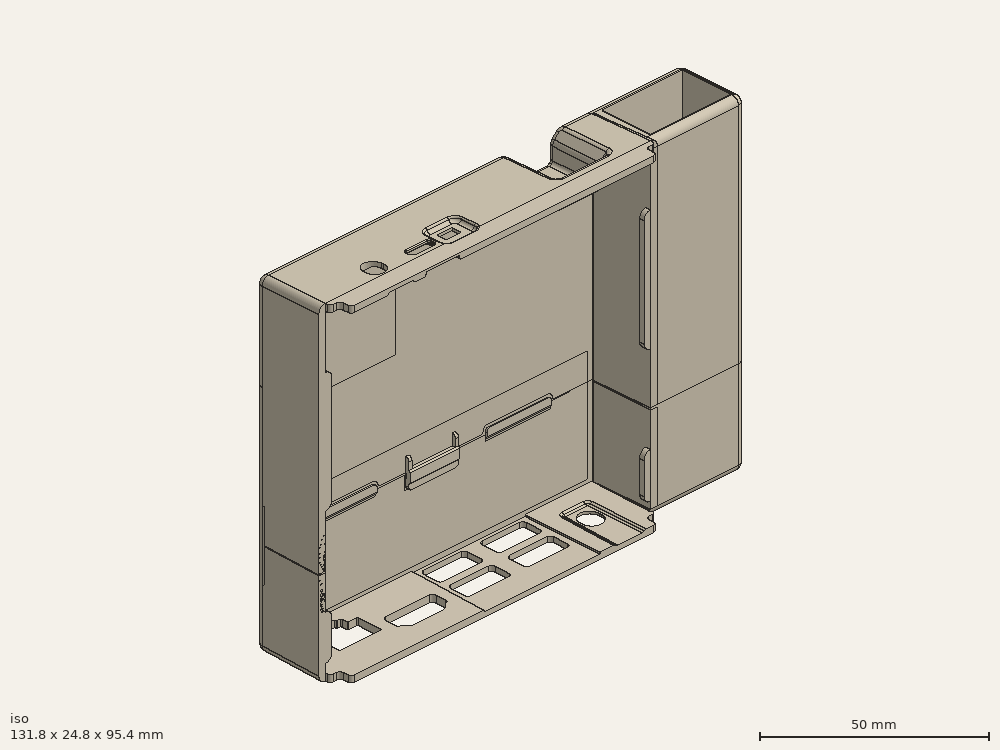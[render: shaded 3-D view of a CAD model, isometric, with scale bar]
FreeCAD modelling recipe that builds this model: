
FCSTD DOCUMENT  (FreeCAD 0.20R29177 +233 (Git))
Label: N2CaseOnePeice_10_12_2022
License: All rights reserved
LicenseURL: http://en.wikipedia.org/wiki/All_rights_reserved
objects: Part::Box×23, Part::Cylinder×12, Part::MultiFuse×10, Part::Cut×9, Part::Sphere×4, Part::Feature×2, Sketcher::SketchObject×2, PartDesign::Pad×2, PartDesign::Body×2
note: 68 computed .brp shape members not serialized (recipe doc carries the construction recipe); baked Part::Feature solids carry a one-line shape summary decoded from their .brp

FEATURE [Part::Feature] Solid  label="N2_BOTTOM_COVER"
  shape: bbox 104.6 x 25.21 x 71.78 mm, 343 faces (baked)
FEATURE [Part::Feature] Solid001  label="N2_TOP_COVER"
  shape: bbox 104.6 x 24.81 x 29.22 mm, 349 faces (baked)
FEATURE [Part::Box] Box  label="Cube"
  AttacherType = Attacher::AttachEngine3D
  Height = 15
  Length = 62.5
  Placement = pos=(-49,18,44) rot=(0,1,0;1.5708rad)
  Width = 2
FEATURE [Part::MultiFuse] Fusion  label="BottomCover"
  Shapes = -> [Solid,Box]
FEATURE [Part::Box] Box001  label="Cube001"
  AttacherType = Attacher::AttachEngine3D
  Height = 15
  Length = 97.5
  Placement = pos=(48.5,20,-3.5) rot=(0,1,0;3.14159rad)
  Width = 2
FEATURE [Part::Cut] Cut
  Base = -> Fusion
  Tool = -> Box001
FEATURE [Part::Box] Box002  label="usbEthernet"
  AttacherType = Attacher::AttachEngine3D
  Height = 25
  Length = 72
  Placement = pos=(52.5,2.6,47.4) rot=(0,1,0;1.5708rad)
  Width = 15
FEATURE [Part::Box] Box003  label="usbEthernetCover"
  AttacherType = Attacher::AttachEngine3D
  Height = 27.5
  Length = 72
  Placement = pos=(50.5,2.2,47.4) rot=(0,1,0;1.5708rad)
  Width = 15.85
FEATURE [Part::Box] Box004  label="usbEthernetCover001"
  AttacherType = Attacher::AttachEngine3D
  Height = 27.52
  Length = 65.19
  Placement = pos=(49.98,17.6,45.39) rot=(0,1,0;1.5708rad)
  Width = 2.4
FEATURE [Part::Box] Box005  label="usbEthernetCover002"
  AttacherType = Attacher::AttachEngine3D
  Height = 2
  Length = 65.19
  Placement = pos=(77.5,2.2,45.39) rot=(0,1,0;1.5708rad)
  Width = 15.8
FEATURE [Part::Cylinder] Cylinder
  Angle = 90
  AttacherType = Attacher::AttachEngine3D
  FirstAngle = 0
  Height = 65.2
  Placement = pos=(77.5,2.2,-19.8) rot=(0,0,-1;1.5708rad)
  Radius = 2
  SecondAngle = 0
FEATURE [Part::Cylinder] Cylinder001
  Angle = 90
  AttacherType = Attacher::AttachEngine3D
  FirstAngle = 0
  Height = 27.5
  Placement = pos=(77.5,18,45.4) rot=(0,-1,0;1.5708rad)
  Radius = 2
  SecondAngle = 0
FEATURE [Part::Cylinder] Cylinder002
  Angle = 90
  AttacherType = Attacher::AttachEngine3D
  FirstAngle = 0
  Height = 15.8
  Placement = pos=(77.5,2.2,45.4) rot=(0.57735,0.57735,0.57735;4.18879rad)
  Radius = 2
  SecondAngle = 0
FEATURE [Part::Cylinder] Cylinder003
  Angle = 90
  AttacherType = Attacher::AttachEngine3D
  FirstAngle = 0
  Height = 65.2
  Placement = pos=(77.5,18,-19.8) rot=(0,0,1;0rad)
  Radius = 2
  SecondAngle = 0
FEATURE [Part::Box] Box006  label="usbEthernetCover003"
  AttacherType = Attacher::AttachEngine3D
  Height = 27.2
  Length = 65.19
  Placement = pos=(50.3,0.2,45.39) rot=(0,1,0;1.5708rad)
  Width = 2.4
FEATURE [Part::Cylinder] Cylinder004
  Angle = 90
  AttacherType = Attacher::AttachEngine3D
  FirstAngle = 0
  Height = 26.4
  Placement = pos=(77.5,2.2,45.4) rot=(0.57735,-0.57735,-0.57735;2.0944rad)
  Radius = 2
  SecondAngle = 0
FEATURE [Part::Sphere] Sphere
  Angle1 = -90
  Angle2 = 90
  Angle3 = 360
  AttacherType = Attacher::AttachEngine3D
  Placement = pos=(77.5,18,45.4) rot=(0,0,1;0rad)
  Radius = 2
FEATURE [Part::Sphere] Sphere001
  Angle1 = -90
  Angle2 = 90
  Angle3 = 360
  AttacherType = Attacher::AttachEngine3D
  Placement = pos=(77.5,2.2,45.4) rot=(0,0,1;0rad)
  Radius = 2
FEATURE [Part::MultiFuse] Fusion001  label="usbCover"
  Shapes = -> [Box003,Box004,Box005,Cylinder,Cylinder001,Cylinder002,Cylinder003,Box006,Cylinder004,Sphere,Sphere001]
FEATURE [Part::MultiFuse] Fusion002
  Shapes = -> [Cut,Fusion001]
FEATURE [Part::Cut] Cut001  label="front"
  Base = -> Fusion002
  Tool = -> Box002
FEATURE [Part::Box] Box007  label="Cube002"
  AttacherType = Attacher::AttachEngine3D
  Height = 10
  Length = 30
  Placement = pos=(79.5,0,-19.8) rot=(0,1,0;3.14159rad)
  Width = 20
FEATURE [Part::Cut] Cut002
  Base = -> Cut001
  Tool = -> Box007
FEATURE [Part::Box] Box008  label="Cube003"
  AttacherType = Attacher::AttachEngine3D
  Height = 10
  Length = 30
  Placement = pos=(79.5,0,-19.8) rot=(0,1,0;3.14159rad)
  Width = 20
FEATURE [Part::Cut] Cut003  label="front001"
  Base = -> Cut002
  Tool = -> Box008
FEATURE [Part::Box] Box009  label="usbEthernet001"
  AttacherType = Attacher::AttachEngine3D
  Height = 25
  Length = 72
  Placement = pos=(52.5,2.6,6.3) rot=(0,1,0;1.5708rad)
  Width = 15
FEATURE [Part::Box] Box010  label="usbEthernetCover004"
  AttacherType = Attacher::AttachEngine3D
  Height = 27.5
  Length = 72
  Placement = pos=(50.5,2.2,-19.8) rot=(0,1,0;1.5708rad)
  Width = 15.85
FEATURE [Part::Box] Box011  label="usbEthernetCover005"
  AttacherType = Attacher::AttachEngine3D
  Height = 27.52
  Length = 65.19
  Placement = pos=(49.98,17.6,-19.8) rot=(0,1,0;1.5708rad)
  Width = 2.4
FEATURE [Part::Box] Box012  label="usbEthernetCover006"
  AttacherType = Attacher::AttachEngine3D
  Height = 2
  Length = 65.19
  Placement = pos=(77.5,2.2,-19.8) rot=(0,1,0;1.5708rad)
  Width = 15.8
FEATURE [Part::Box] Box013  label="usbEthernetCover007"
  AttacherType = Attacher::AttachEngine3D
  Height = 27.2
  Length = 65.19
  Placement = pos=(50.3,0.2,-19.8) rot=(0,1,0;1.5708rad)
  Width = 2.4
FEATURE [Part::Box] Box016  label="Cube005"
  AttacherType = Attacher::AttachEngine3D
  Height = 50
  Length = 29.5
  Placement = pos=(79.5,0,-45.4) rot=(0,1,0;3.14159rad)
  Width = 20
FEATURE [Part::MultiFuse] Fusion003
  Shapes = -> [Solid001,Box010,Box011,Box012,Box013]
FEATURE [Part::Cut] Cut004
  Base = -> Fusion003
  Tool = -> Box016
FEATURE [Part::Cut] Cut005
  Base = -> Cut004
  Tool = -> Box009
FEATURE [Part::Box] Box017  label="Cube006"
  AttacherType = Attacher::AttachEngine3D
  Height = 50
  Length = 23.5
  Placement = pos=(73.4,17.6,-45.39) rot=(0,1,0;3.14159rad)
  Width = 20
FEATURE [Part::Cut] Cut006
  Base = -> Cut005
  Tool = -> Box017
FEATURE [Part::Cylinder] Cylinder005
  Angle = 90
  AttacherType = Attacher::AttachEngine3D
  FirstAngle = 0
  Height = 65.2
  Placement = pos=(77.5,2.2,-45.4) rot=(0,0,-1;1.5708rad)
  Radius = 2
  SecondAngle = 0
FEATURE [Part::Cylinder] Cylinder006
  Angle = 90
  AttacherType = Attacher::AttachEngine3D
  FirstAngle = 0
  Height = 27.5
  Placement = pos=(77.5,18,-45.4) rot=(0,-1,0;1.5708rad)
  Radius = 2
  SecondAngle = 0
FEATURE [Part::Cylinder] Cylinder007
  Angle = 90
  AttacherType = Attacher::AttachEngine3D
  FirstAngle = 0
  Height = 15.8
  Placement = pos=(77.5,2.2,-45.4) rot=(-1,0,0;1.5708rad)
  Radius = 2
  SecondAngle = 0
FEATURE [Part::Cylinder] Cylinder008
  Angle = 90
  AttacherType = Attacher::AttachEngine3D
  FirstAngle = 0
  Height = 65.2
  Placement = pos=(77.5,18,-45.4) rot=(0,0,1;0rad)
  Radius = 2
  SecondAngle = 0
FEATURE [Part::Cylinder] Cylinder009
  Angle = 90
  AttacherType = Attacher::AttachEngine3D
  FirstAngle = 0
  Height = 27.6
  Placement = pos=(77.5,2.2,-45.4) rot=(0.707107,0,-0.707107;3.14159rad)
  Radius = 2
  SecondAngle = 0
FEATURE [Part::Cylinder] Cylinder010
  Angle = 90
  AttacherType = Attacher::AttachEngine3D
  FirstAngle = 0
  Height = 27.6
  Placement = pos=(77.5,18,-45.4) rot=(0.57735,0.57735,-0.57735;4.18879rad)
  Radius = 2
  SecondAngle = 0
FEATURE [Part::Box] Box018  label="Cube007"
  AttacherType = Attacher::AttachEngine3D
  Height = 2
  Length = 27.6
  Placement = pos=(49.9,18,-45.4) rot=(1,0,0;3.14159rad)
  Width = 15.8
FEATURE [Part::Box] Box019  label="usbEthernet002"
  AttacherType = Attacher::AttachEngine3D
  Height = 25
  Length = 72
  Placement = pos=(52.5,2.6,-2.5) rot=(0,1,0;1.5708rad)
  Width = 15
FEATURE [Part::Sphere] Sphere002
  Angle1 = -90
  Angle2 = 90
  Angle3 = 360
  AttacherType = Attacher::AttachEngine3D
  Placement = pos=(77.5,18,-45.4) rot=(0,0,1;0rad)
  Radius = 2
FEATURE [Part::Sphere] Sphere003
  Angle1 = -90
  Angle2 = 90
  Angle3 = 360
  AttacherType = Attacher::AttachEngine3D
  Placement = pos=(77.5,2.2,-45.4) rot=(0,0,1;0rad)
  Radius = 2
FEATURE [Part::Box] Box020  label="Cube008"
  AttacherType = Attacher::AttachEngine3D
  Height = 40
  Length = 10
  Placement = pos=(73.6,0,-19.8) rot=(0,0,1;0rad)
  Width = 22
FEATURE [Part::MultiFuse] Fusion004  label="cuts"
  Shapes = -> [Box020,Box019]
FEATURE [Part::MultiFuse] Fusion005
  Shapes = -> [Sphere003,Cut006,Cylinder005,Cylinder006,Cylinder007,Cylinder008,Cylinder009,Cylinder010,Box018,Sphere002]
FEATURE [Part::Cut] Cut007  label="back"
  Base = -> Fusion005
  Tool = -> Fusion004
FEATURE [Part::Box] Box021  label="Cube009"
  AttacherType = Attacher::AttachEngine3D
  Height = 32.5
  Length = 97.5
  Placement = pos=(48.5,18,-11.9) rot=(0,1,0;3.14159rad)
  Width = 2
FEATURE [Part::Box] Box068  label="logoBase001"
  AttacherType = Attacher::AttachEngine3D
  Height = 30
  Length = 35
  Placement = pos=(21.5,-44,15.25) rot=(0,0,1;0rad)
  Width = 1.8
FEATURE [Sketcher::SketchObject] Sketch001
  FullyConstrained = false
  MapMode = 5
  Support = -> [XY_Plane001]
  sketch-geometry (205):
    g0: LineSegment StartX=-15.0667 StartY=-2.9879 StartZ=0 EndX=-14.4175 EndY=-3.20194 EndZ=0
    g1: LineSegment StartX=-14.1386 StartY=-3.3581 StartZ=0 EndX=-13.8673 EndY=-3.55064 EndZ=0
    g2: LineSegment StartX=-10.8098 StartY=-4.00788 StartZ=0 EndX=-10.5716 EndY=-4.29909 EndZ=0
    g3: LineSegment StartX=-10.5716 StartY=-4.29909 StartZ=0 EndX=-10.1338 EndY=-4.33136 EndZ=0
    g4: LineSegment StartX=-10.1338 StartY=-4.33136 StartZ=0 EndX=-9.89036 EndY=-4.3898 EndZ=0
    g5: LineSegment StartX=-9.51656 StartY=-5.73022 StartZ=0 EndX=-9.24931 EndY=-5.76229 EndZ=0
    g6: LineSegment StartX=-9.24931 StartY=-5.76229 StartZ=0 EndX=-8.92861 EndY=-5.90126 EndZ=0
    g7: LineSegment StartX=-8.92861 StartY=-5.90126 StartZ=0 EndX=-8.54378 EndY=-5.86384 EndZ=0
    g8: LineSegment StartX=-8.54378 StartY=-5.86384 StartZ=0 EndX=-7.71788 EndY=-5.75845 EndZ=0
    g9: LineSegment StartX=-7.71788 StartY=-5.75845 StartZ=0 EndX=-7.37291 EndY=-5.97257 EndZ=0
    g10: LineSegment StartX=-7.37291 StartY=-5.97257 StartZ=0 EndX=-6.72487 EndY=-5.72038 EndZ=0
    g11: LineSegment StartX=-6.72487 StartY=-5.72038 StartZ=0 EndX=-6.27066 EndY=-5.69481 EndZ=0
    g12: LineSegment StartX=-6.27066 StartY=-5.69481 StartZ=0 EndX=-6.06223 EndY=-5.80493 EndZ=0
    g13: LineSegment StartX=-6.06223 StartY=-5.80493 StartZ=0 EndX=-5.35089 EndY=-5.48914 EndZ=0
    g14: LineSegment StartX=-5.35089 StartY=-5.48914 StartZ=0 EndX=-5.02402 EndY=-5.48914 EndZ=0
    g15: LineSegment StartX=-5.02402 StartY=-5.48914 StartZ=0 EndX=-4.80126 EndY=-5.53132 EndZ=0
    g16: LineSegment StartX=-4.80126 StartY=-5.53132 StartZ=0 EndX=-4.19735 EndY=-5.16248 EndZ=0
    g17: LineSegment StartX=-3.75191 StartY=-4.97251 StartZ=0 EndX=-3.37714 EndY=-4.97251 EndZ=0
    g18: LineSegment StartX=-3.37714 StartY=-4.97251 StartZ=0 EndX=-2.81898 EndY=-4.45422 EndZ=0
    g19: LineSegment StartX=-2.81898 StartY=-4.45422 StartZ=0 EndX=-2.62761 EndY=-4.34259 EndZ=0
    g20: LineSegment StartX=-2.62761 StartY=-4.34259 StartZ=0 EndX=-2.15112 EndY=-4.35765 EndZ=0
    g21: LineSegment StartX=-2.38042 StartY=-4.51801 StartZ=0 EndX=-3.18577 EndY=-5.42702 EndZ=0
    g22: LineSegment StartX=-3.18577 StartY=-5.42702 StartZ=0 EndX=-3.61318 EndY=-6.05824 EndZ=0
    g23: LineSegment StartX=-3.61318 StartY=-6.05824 StartZ=0 EndX=-3.7111 EndY=-6.64579 EndZ=0
    g24: LineSegment StartX=-3.7111 StartY=-6.64579 StartZ=0 EndX=-3.83514 EndY=-7.15501 EndZ=0
    g25: LineSegment StartX=-3.83514 StartY=-7.15501 StartZ=0 EndX=-3.75878 EndY=-7.50876 EndZ=0
    g26: LineSegment StartX=-3.75878 StartY=-7.50876 StartZ=0 EndX=-3.70596 EndY=-7.68135 EndZ=0
    g27: LineSegment StartX=-3.70596 StartY=-7.68135 StartZ=0 EndX=-3.53967 EndY=-7.85202 EndZ=0
    g28: LineSegment StartX=-3.53967 StartY=-7.85202 StartZ=0 EndX=-3.4685 EndY=-8.65617 EndZ=0
    g29: LineSegment StartX=-3.27268 StartY=-8.56671 StartZ=0 EndX=-3.16823 EndY=-8.76909 EndZ=0
    g30: LineSegment StartX=-3.07088 StartY=-9.32083 StartZ=0 EndX=-2.84207 EndY=-9.3355 EndZ=0
    g31: LineSegment StartX=-2.84207 StartY=-9.3355 StartZ=0 EndX=-2.45193 EndY=-10.0982 EndZ=0
    g32: LineSegment StartX=-2.45193 StartY=-10.0982 StartZ=0 EndX=-2.24953 EndY=-10.1304 EndZ=0
    g33: LineSegment StartX=-2.24953 StartY=-10.1304 StartZ=0 EndX=-0.96042 EndY=-11.8753 EndZ=0
    g34: LineSegment StartX=-0.96042 StartY=-11.8753 StartZ=0 EndX=-0.153326 EndY=-11.3889 EndZ=0
    g35: LineSegment StartX=-0.153326 StartY=-11.3889 StartZ=0 EndX=0.461347 EndY=-10.7689 EndZ=0
    g36: LineSegment StartX=0.461347 StartY=-10.7689 StartZ=0 EndX=0.669802 EndY=-10.7261 EndZ=0
    g37: LineSegment StartX=0.669802 StartY=-10.7261 StartZ=0 EndX=1.31724 EndY=-9.70998 EndZ=0
    g38: LineSegment StartX=1.31724 StartY=-9.70998 StartZ=0 EndX=1.51826 EndY=-9.65081 EndZ=0
    g39: LineSegment StartX=1.51826 StartY=-9.65081 StartZ=0 EndX=1.74022 EndY=-9.08937 EndZ=0
    g40: LineSegment StartX=1.74022 StartY=-9.08937 StartZ=0 EndX=2.02094 EndY=-9.04367 EndZ=0
    g41: LineSegment StartX=2.02094 StartY=-9.04367 StartZ=0 EndX=2.39306 EndY=-7.80327 EndZ=0
    g42: LineSegment StartX=2.39306 StartY=-7.80327 StartZ=0 EndX=2.58839 EndY=-7.69871 EndZ=0
    g43: LineSegment StartX=2.6542 StartY=-7.03945 StartZ=0 EndX=2.86963 EndY=-6.81749 EndZ=0
    g44: LineSegment StartX=2.86963 StartY=-6.81749 StartZ=0 EndX=3.0916 EndY=-6.92847 EndZ=0
    g45: LineSegment StartX=3.0916 StartY=-6.92847 StartZ=0 EndX=3.79666 EndY=-7.57478 EndZ=0
    g46: LineSegment StartX=3.79666 StartY=-7.57478 StartZ=0 EndX=3.93376 EndY=-7.50297 EndZ=0
    g47: LineSegment StartX=3.93376 StartY=-7.50297 StartZ=0 EndX=4.46256 EndY=-7.97301 EndZ=0
    g48: LineSegment StartX=4.46256 StartY=-7.97301 StartZ=0 EndX=4.68452 EndY=-7.92079 EndZ=0
    g49: LineSegment StartX=4.68452 StartY=-7.92079 StartZ=0 EndX=5.1154 EndY=-8.34513 EndZ=0
    g50: LineSegment StartX=5.1154 StartY=-8.34513 StartZ=0 EndX=5.32431 EndY=-8.28637 EndZ=0
    g51: LineSegment StartX=5.32431 StartY=-8.28637 StartZ=0 EndX=6.23668 EndY=-8.79564 EndZ=0
    g52: LineSegment StartX=6.23668 StartY=-8.79564 StartZ=0 EndX=6.50362 EndY=-8.76631 EndZ=0
    g53: LineSegment StartX=6.50362 StartY=-8.76631 StartZ=0 EndX=7.14802 EndY=-9.05537 EndZ=0
    g54: LineSegment StartX=7.14802 StartY=-9.05537 StartZ=0 EndX=8.04883 EndY=-9.18613 EndZ=0
    g55: LineSegment StartX=8.04883 StartY=-9.18613 StartZ=0 EndX=8.36847 EndY=-7.93662 EndZ=0
    g56: LineSegment StartX=8.36847 StartY=-7.93662 StartZ=0 EndX=8.49923 EndY=-7.79133 EndZ=0
    g57: LineSegment StartX=8.49923 StartY=-7.79133 StartZ=0 EndX=8.43477 EndY=-6.72206 EndZ=0
    g58: LineSegment StartX=8.43477 StartY=-6.72206 StartZ=0 EndX=8.58621 EndY=-6.47988 EndZ=0
    g59: LineSegment StartX=8.58621 StartY=-6.47988 StartZ=0 EndX=8.32296 EndY=-5.53178 EndZ=0
    g60: LineSegment StartX=8.32296 StartY=-5.53178 StartZ=0 EndX=8.43984 EndY=-5.19091 EndZ=0
    g61: LineSegment StartX=8.43984 StartY=-5.19091 StartZ=0 EndX=8.07426 EndY=-4.39307 EndZ=0
    g62: LineSegment StartX=8.07426 StartY=-4.39307 StartZ=0 EndX=8.04236 EndY=-4.17777 EndZ=0
    g63: LineSegment StartX=8.04236 StartY=-4.17777 StartZ=0 EndX=8.0902 EndY=-3.99438 EndZ=0
    g64: LineSegment StartX=8.4103 StartY=-4.11103 StartZ=0 EndX=8.72013 EndY=-4.0502 EndZ=0
    g65: LineSegment StartX=8.72013 StartY=-4.0502 StartZ=0 EndX=9.31817 EndY=-4.0502 EndZ=0
    g66: LineSegment StartX=9.31817 StartY=-4.0502 StartZ=0 EndX=9.82964 EndY=-4.15887 EndZ=0
    g67: LineSegment StartX=10.1326 StartY=-3.9675 StartZ=0 EndX=10.5175 EndY=-3.9623 EndZ=0
    g68: LineSegment StartX=10.5175 StartY=-3.9623 StartZ=0 EndX=10.8831 EndY=-3.97536 EndZ=0
    g69: LineSegment StartX=10.8831 StartY=-3.97536 StartZ=0 EndX=11.2245 EndY=-4.09431 EndZ=0
    g70: LineSegment StartX=11.2245 StartY=-4.09431 StartZ=0 EndX=11.6861 EndY=-3.91007 EndZ=0
    g71: LineSegment StartX=11.6861 StartY=-3.91007 StartZ=0 EndX=12.1039 EndY=-3.88396 EndZ=0
    g72: LineSegment StartX=12.1039 StartY=-3.88396 StartZ=0 EndX=12.6 EndY=-3.9623 EndZ=0
    g73: LineSegment StartX=12.6 StartY=-3.9623 StartZ=0 EndX=13.5793 EndY=-3.87743 EndZ=0
    g74: LineSegment StartX=13.5793 StartY=-3.87743 StartZ=0 EndX=14.3888 EndY=-3.74687 EndZ=0
    g75: LineSegment StartX=14.3888 StartY=-3.74687 StartZ=0 EndX=14.7544 EndY=-3.68158 EndZ=0
    g76: LineSegment StartX=14.7544 StartY=-3.68158 StartZ=0 EndX=15.2767 EndY=-3.75339 EndZ=0
    g77: LineSegment StartX=15.2767 StartY=-3.75339 StartZ=0 EndX=15.0432 EndY=-3.24137 EndZ=0
    g78: LineSegment StartX=15.0432 StartY=-3.24137 StartZ=0 EndX=14.5209 EndY=-2.51672 EndZ=0
    g79: LineSegment StartX=14.5209 StartY=-2.51672 StartZ=0 EndX=14.0378 EndY=-1.99445 EndZ=0
    g80: LineSegment StartX=14.0378 StartY=-1.99445 StartZ=0 EndX=13.2802 EndY=-1.54625 EndZ=0
    g81: LineSegment StartX=13.2802 StartY=-1.54625 StartZ=0 EndX=13.0438 EndY=-1.23117 EndZ=0
    g82: LineSegment StartX=13.0438 StartY=-1.23117 StartZ=0 EndX=12.1074 EndY=-0.797939 EndZ=0
    g83: LineSegment StartX=12.1074 StartY=-0.797939 StartZ=0 EndX=11.3804 EndY=-0.250878 EndZ=0
    g84: LineSegment StartX=11.3804 StartY=-0.250878 StartZ=0 EndX=10.4396 EndY=0.304889 EndZ=0
    g85: LineSegment StartX=10.4396 StartY=0.304889 StartZ=0 EndX=9.59526 EndY=0.727998 EndZ=0
    g86: LineSegment StartX=9.59526 StartY=0.727998 StartZ=0 EndX=8.53624 EndY=0.97306 EndZ=0
    g87: LineSegment StartX=8.53624 StartY=0.97306 StartZ=0 EndX=7.199 EndY=0.97306 EndZ=0
    g88: LineSegment StartX=7.199 StartY=0.97306 StartZ=0 EndX=5.77932 EndY=0.795578 EndZ=0
    g89: LineSegment StartX=5.77932 StartY=0.795578 StartZ=0 EndX=5.60186 EndY=0.795578 EndZ=0
    g90: LineSegment StartX=5.60186 StartY=0.795578 StartZ=0 EndX=5.83178 EndY=0.981815 EndZ=0
    g91: LineSegment StartX=5.83178 StartY=0.981815 StartZ=0 EndX=6.25403 EndY=1.1582 EndZ=0
    g92: LineSegment StartX=6.30214 StartY=1.38269 StartZ=0 EndX=7.17987 EndY=1.70686 EndZ=0
    g93: LineSegment StartX=7.17987 StartY=1.70686 StartZ=0 EndX=7.44682 EndY=1.79438 EndZ=0
    g94: LineSegment StartX=7.44682 StartY=1.79438 StartZ=0 EndX=7.49058 EndY=2.12696 EndZ=0
    g95: LineSegment StartX=7.49058 StartY=2.12696 StartZ=0 EndX=8.30058 EndY=2.66839 EndZ=0
    g96: LineSegment StartX=8.30058 StartY=2.66839 StartZ=0 EndX=8.68575 EndY=2.81854 EndZ=0
    g97: LineSegment StartX=8.68575 StartY=2.81854 StartZ=0 EndX=8.68575 EndY=3.12537 EndZ=0
    g98: LineSegment StartX=8.68575 StartY=3.12537 StartZ=0 EndX=8.89508 EndY=3.18684 EndZ=0
    g99: LineSegment StartX=8.89508 StartY=3.18684 StartZ=0 EndX=9.63492 EndY=4.06602 EndZ=0
    g100: LineSegment StartX=9.63492 StartY=4.06602 StartZ=0 EndX=9.62638 EndY=4.32743 EndZ=0
    g101: LineSegment StartX=9.62638 StartY=4.32743 StartZ=0 EndX=10.2068 EndY=5.18314 EndZ=0
    g102: LineSegment StartX=10.2068 StartY=5.18314 StartZ=0 EndX=9.25518 EndY=5.64445 EndZ=0
    g103: LineSegment StartX=9.1102 StartY=5.87597 StartZ=0 EndX=8.32132 EndY=5.97336 EndZ=0
    g104: LineSegment StartX=8.32132 StartY=5.97336 StartZ=0 EndX=8.15466 EndY=6.06625 EndZ=0
    g105: LineSegment StartX=7.63471 StartY=6.13088 StartZ=0 EndX=7.56391 EndY=6.33267 EndZ=0
    g106: LineSegment StartX=7.56391 StartY=6.33267 StartZ=0 EndX=6.74832 EndY=6.35496 EndZ=0
    g107: LineSegment StartX=6.74832 StartY=6.35496 StartZ=0 EndX=6.46819 EndY=6.29526 EndZ=0
    g108: LineSegment StartX=6.46819 StartY=6.29526 StartZ=0 EndX=6.27042 EndY=6.61061 EndZ=0
    g109: LineSegment StartX=6.27042 StartY=6.61061 StartZ=0 EndX=5.40453 EndY=6.33267 EndZ=0
    g110: LineSegment StartX=5.40453 StartY=6.33267 StartZ=0 EndX=5.27091 EndY=6.47164 EndZ=0
    g111: LineSegment StartX=5.27091 StartY=6.47164 StartZ=0 EndX=4.56942 EndY=6.24725 EndZ=0
    g112: LineSegment StartX=4.56942 StartY=6.24725 StartZ=0 EndX=4.44161 EndY=6.40652 EndZ=0
    g113: LineSegment StartX=4.44161 StartY=6.40652 StartZ=0 EndX=3.4195 EndY=5.94588 EndZ=0
    g114: LineSegment StartX=3.4195 StartY=5.94588 StartZ=0 EndX=3.29192 EndY=6.1532 EndZ=0
    g115: LineSegment StartX=3.29192 StartY=6.1532 StartZ=0 EndX=2.15964 EndY=5.49137 EndZ=0
    g116: LineSegment StartX=2.15964 StartY=5.49137 StartZ=0 EndX=2.00016 EndY=5.69869 EndZ=0
    g117: LineSegment StartX=2.00016 StartY=5.69869 StartZ=0 EndX=1.6185 EndY=5.34828 EndZ=0
    g118: LineSegment StartX=1.6185 StartY=5.34828 StartZ=0 EndX=1.45984 EndY=5.94974 EndZ=0
    g119: LineSegment StartX=1.38165 StartY=6.28651 StartZ=0 EndX=1.14534 EndY=6.29963 EndZ=0
    g120: LineSegment StartX=0.348522 StartY=7.29544 StartZ=0 EndX=0.126706 EndY=7.68126 EndZ=0
    g121: LineSegment StartX=0.126706 StartY=7.68126 StartZ=0 EndX=-0.415308 EndY=8.18163 EndZ=0
    g122: LineSegment StartX=-0.415308 StartY=8.18163 StartZ=0 EndX=-0.872658 EndY=8.6237 EndZ=0
    g123: LineSegment StartX=-0.872658 StartY=8.6237 StartZ=0 EndX=-1.12074 EndY=8.64329 EndZ=0
    g124: LineSegment StartX=-1.12074 StartY=8.64329 StartZ=0 EndX=-1.79316 EndY=9.11986 EndZ=0
    g125: LineSegment StartX=-1.79316 StartY=9.11986 StartZ=0 EndX=-2.31488 EndY=9.12122 EndZ=0
    g126: LineSegment StartX=-2.31488 StartY=9.12122 StartZ=0 EndX=-2.71321 EndY=9.13846 EndZ=0
    g127: LineSegment StartX=-2.71321 StartY=9.13846 StartZ=0 EndX=-2.88425 EndY=9.34157 EndZ=0
    g128: LineSegment StartX=-2.88425 StartY=9.34157 StartZ=0 EndX=-3.16779 EndY=9.26454 EndZ=0
    g129: LineSegment StartX=-3.70739 StartY=9.82796 StartZ=0 EndX=-4.04915 EndY=9.7003 EndZ=0
    g130: LineSegment StartX=-4.04915 StartY=9.7003 StartZ=0 EndX=-4.42988 EndY=10.011 EndZ=0
    g131: LineSegment StartX=-5.98947 StartY=10.3656 StartZ=0 EndX=-7.32605 EndY=10.4108 EndZ=0
    g132: LineSegment StartX=-7.25254 StartY=9.13254 StartZ=0 EndX=-7.36878 EndY=8.7693 EndZ=0
    g133: LineSegment StartX=-7.36878 StartY=8.7693 StartZ=0 EndX=-7.2614 EndY=7.83762 EndZ=0
    g134: LineSegment StartX=-7.2614 StartY=7.83762 StartZ=0 EndX=-7.41112 EndY=7.6042 EndZ=0
    g135: LineSegment StartX=-7.41112 StartY=7.6042 StartZ=0 EndX=-7.09216 EndY=6.74302 EndZ=0
    g136: LineSegment StartX=-7.09216 StartY=6.74302 StartZ=0 EndX=-7.10014 EndY=6.55962 EndZ=0
    g137: LineSegment StartX=-7.10014 StartY=6.55962 StartZ=0 EndX=-7.29151 EndY=6.3842 EndZ=0
    g138: LineSegment StartX=-7.29151 StartY=6.3842 StartZ=0 EndX=-6.74132 EndY=5.29976 EndZ=0
    g139: LineSegment StartX=-6.74132 StartY=5.29976 StartZ=0 EndX=-6.87495 EndY=5.02732 EndZ=0
    g140: LineSegment StartX=-6.87495 StartY=5.02732 StartZ=0 EndX=-6.31586 EndY=4.42065 EndZ=0
    g141: LineSegment StartX=-6.31586 StartY=4.42065 StartZ=0 EndX=-6.30396 EndY=4.19463 EndZ=0
    g142: LineSegment StartX=-6.30396 StartY=4.19463 StartZ=0 EndX=-6.05415 EndY=4.0043 EndZ=0
    g143: LineSegment StartX=-6.05415 StartY=4.0043 StartZ=0 EndX=-6.18501 EndY=3.95672 EndZ=0
    g144: LineSegment StartX=-6.18501 StartY=3.95672 StartZ=0 EndX=-5.54265 EndY=3.07645 EndZ=0
    g145: LineSegment StartX=-5.54265 StartY=3.07645 StartZ=0 EndX=-5.57833 EndY=2.90991 EndZ=0
    g146: LineSegment StartX=-5.57833 StartY=2.90991 StartZ=0 EndX=-5.1263 EndY=2.41029 EndZ=0
    g147: LineSegment StartX=-5.1263 StartY=2.41029 StartZ=0 EndX=-5.18578 EndY=2.26755 EndZ=0
    g148: LineSegment StartX=-5.18578 StartY=2.26755 StartZ=0 EndX=-4.73375 EndY=1.89878 EndZ=0
    g149: LineSegment StartX=-4.73375 StartY=1.89878 StartZ=0 EndX=-4.42446 EndY=1.5895 EndZ=0
    g150: LineSegment StartX=-4.42446 StartY=1.5895 StartZ=0 EndX=-5.31663 EndY=1.29211 EndZ=0
    g151: LineSegment StartX=-5.31663 StartY=1.29211 StartZ=0 EndX=-5.84004 EndY=1.08988 EndZ=0
    g152: LineSegment StartX=-5.84004 StartY=1.08988 StartZ=0 EndX=-6.04226 EndY=0.792495 EndZ=0
    g153: LineSegment StartX=-6.04226 StartY=0.792495 StartZ=0 EndX=-6.94632 EndY=0.994719 EndZ=0
    g154: LineSegment StartX=-6.94632 StartY=0.994719 StartZ=0 EndX=-7.19613 EndY=0.887659 EndZ=0
    g155: LineSegment StartX=-7.19613 StartY=0.887659 StartZ=0 EndX=-7.8147 EndY=1.0423 EndZ=0
    g156: LineSegment StartX=-7.8147 StartY=1.0423 StartZ=0 EndX=-8.02502 EndY=0.969153 EndZ=0
    g157: LineSegment StartX=-8.02502 StartY=0.969153 StartZ=0 EndX=-8.60267 EndY=1.03042 EndZ=0
    g158: LineSegment StartX=-8.60267 StartY=1.03042 StartZ=0 EndX=-8.8346 EndY=0.872878 EndZ=0
    g159: LineSegment StartX=-8.8346 StartY=0.872878 StartZ=0 EndX=-9.33349 EndY=0.929767 EndZ=0
    g160: LineSegment StartX=-9.33349 StartY=0.929767 StartZ=0 EndX=-9.66169 EndY=0.649695 EndZ=0
    g161: LineSegment StartX=-9.66169 StartY=0.649695 StartZ=0 EndX=-10.3249 EndY=0.649695 EndZ=0
    g162: LineSegment StartX=-10.3249 StartY=0.649695 StartZ=0 EndX=-11.0107 EndY=0.32425 EndZ=0
    g163: LineSegment StartX=-11.0107 StartY=0.32425 StartZ=0 EndX=-11.7283 EndY=0.053139 EndZ=0
    g164: LineSegment StartX=-11.7283 StartY=0.053139 StartZ=0 EndX=-12.2971 EndY=-0.13161 EndZ=0
    g165: LineSegment StartX=-12.2971 StartY=-0.13161 StartZ=0 EndX=-12.4212 EndY=-0.347049 EndZ=0
    g166: LineSegment StartX=-12.4212 StartY=-0.347049 StartZ=0 EndX=-13.296 EndY=-0.817096 EndZ=0
    g167: LineSegment StartX=-13.296 StartY=-0.817096 StartZ=0 EndX=-13.9227 EndY=-1.24144 EndZ=0
    g168: LineSegment StartX=-13.9227 StartY=-1.24144 StartZ=0 EndX=-14.1708 EndY=-1.59398 EndZ=0
    g169: LineSegment StartX=-14.1708 StartY=-1.59398 StartZ=0 EndX=-14.5386 EndY=-2.09216 EndZ=0
    g170: LineSegment StartX=-14.5386 StartY=-2.09216 StartZ=0 EndX=-14.7831 EndY=-2.4577 EndZ=0
    g171: LineSegment StartX=-14.7831 StartY=-2.4577 StartZ=0 EndX=-15.0667 EndY=-2.9879 EndZ=0
    g172: LineSegment StartX=7.82861 StartY=6.04487 StartZ=0 EndX=7.63471 EndY=6.13088 EndZ=0
    g173: LineSegment StartX=-14.4175 StartY=-3.20194 StartZ=0 EndX=-14.1386 EndY=-3.3581 EndZ=0
    g174: LineSegment StartX=-13.8673 StartY=-3.55064 StartZ=0 EndX=-13.4107 EndY=-3.57136 EndZ=0
    g175: LineSegment StartX=-13.1321 StartY=-3.61699 StartZ=0 EndX=-12.817 EndY=-3.62343 EndZ=0
    g176: LineSegment StartX=-12.817 StartY=-3.62343 StartZ=0 EndX=-12.4662 EndY=-3.85302 EndZ=0
    g177: LineSegment StartX=-13.4107 StartY=-3.57136 StartZ=0 EndX=-13.1321 EndY=-3.61699 EndZ=0
    g178: LineSegment StartX=-12.4662 StartY=-3.85302 StartZ=0 EndX=-11.8704 EndY=-3.85302 EndZ=0
    g179: LineSegment StartX=-11.8704 StartY=-3.85302 StartZ=0 EndX=-11.5204 EndY=-4.00836 EndZ=0
    g180: LineSegment StartX=-11.5204 StartY=-4.00836 StartZ=0 EndX=-11.1389 EndY=-4.05555 EndZ=0
    g181: LineSegment StartX=-11.1389 StartY=-4.05555 StartZ=0 EndX=-10.8098 EndY=-4.00788 EndZ=0
    g182: LineSegment StartX=-9.89036 StartY=-4.3898 StartZ=0 EndX=-9.99555 EndY=-4.87697 EndZ=0
    g183: LineSegment StartX=-9.99555 StartY=-4.87697 StartZ=0 EndX=-10.0894 EndY=-5.36391 EndZ=0
    g184: LineSegment StartX=-10.0894 StartY=-5.36391 StartZ=0 EndX=-10.107 EndY=-5.50471 EndZ=0
    g185: LineSegment StartX=-10.107 StartY=-5.50471 StartZ=0 EndX=-9.77848 EndY=-5.63965 EndZ=0
    g186: LineSegment StartX=-9.77848 StartY=-5.63965 StartZ=0 EndX=-9.51656 EndY=-5.73022 EndZ=0
    g187: LineSegment StartX=-4.19735 StartY=-5.16248 StartZ=0 EndX=-3.75191 EndY=-4.97251 EndZ=0
    g188: LineSegment StartX=-2.38042 StartY=-4.51801 StartZ=0 EndX=-2.15112 EndY=-4.35765 EndZ=0
    g189: LineSegment StartX=-3.4685 StartY=-8.65617 StartZ=0 EndX=-3.27268 EndY=-8.56671 EndZ=0
    g190: LineSegment StartX=-3.16823 StartY=-8.76909 StartZ=0 EndX=-3.07088 EndY=-9.32083 EndZ=0
    g191: LineSegment StartX=2.58839 StartY=-7.69871 StartZ=0 EndX=2.6542 EndY=-7.03945 EndZ=0
    g192: LineSegment StartX=8.0902 StartY=-3.99438 StartZ=0 EndX=8.4103 EndY=-4.11103 EndZ=0
    g193: LineSegment StartX=9.82964 StartY=-4.15887 StartZ=0 EndX=10.1326 EndY=-3.9675 EndZ=0
    g194: LineSegment StartX=6.30214 StartY=1.38269 StartZ=0 EndX=6.25403 EndY=1.1582 EndZ=0
    g195: LineSegment StartX=1.38165 StartY=6.28651 StartZ=0 EndX=1.45984 EndY=5.94974 EndZ=0
    g196: LineSegment StartX=0.348522 StartY=7.29544 StartZ=0 EndX=0.824344 EndY=6.91479 EndZ=0
    g197: LineSegment StartX=0.824344 StartY=6.91479 StartZ=0 EndX=1.14534 EndY=6.29963 EndZ=0
    g198: LineSegment StartX=-3.70739 StartY=9.82796 StartZ=0 EndX=-3.16779 EndY=9.26454 EndZ=0
    g199: LineSegment StartX=-5.98947 StartY=10.3656 StartZ=0 EndX=-5.43038 EndY=10.4489 EndZ=0
    g200: LineSegment StartX=-5.43038 StartY=10.4489 StartZ=0 EndX=-4.9791 EndY=10.1425 EndZ=0
    g201: LineSegment StartX=-4.42988 StartY=10.011 StartZ=0 EndX=-4.9791 EndY=10.1425 EndZ=0
    g202: LineSegment StartX=-7.25254 StartY=9.13254 StartZ=0 EndX=-7.32605 EndY=10.4108 EndZ=0
    g203: LineSegment StartX=7.82861 StartY=6.04487 StartZ=0 EndX=8.15466 EndY=6.06625 EndZ=0
    g204: LineSegment StartX=9.1102 StartY=5.87597 StartZ=0 EndX=9.25518 EndY=5.64445 EndZ=0
  constraints (114):
    c: Coincident(g4,g3)
    c: Coincident(g6,g5)
    c: Coincident(g8,g7)
    c: Coincident(g9,g8)
    c: Coincident(g10,g9)
    c: Coincident(g11,g10)
    c: Coincident(g13,g12)
    c: Coincident(g16,g15)
    c: Coincident(g22,g21)
    c: Coincident(g25,g24)
    c: Coincident(g26,g25)
    c: Coincident(g28,g27)
    c: Coincident(g33,g32)
    c: Coincident(g37,g36)
    c: Coincident(g38,g37)
    c: Coincident(g40,g39)
    c: Coincident(g44,g43)
    c: Coincident(g51,g50)
    c: Coincident(g52,g51)
    c: Coincident(g57,g56)
    c: Coincident(g58,g57)
    c: Coincident(g59,g58)
    c: Coincident(g61,g60)
    c: Coincident(g63,g62)
    c: Coincident(g66,g65)
    c: Coincident(g70,g69)
    c: Coincident(g72,g71)
    c: Coincident(g73,g72)
    c: Coincident(g74,g73)
    c: Coincident(g77,g76)
    c: Coincident(g80,g79)
    c: Coincident(g81,g80)
    c: Coincident(g83,g82)
    c: Coincident(g85,g84)
    c: Coincident(g86,g85)
    c: Coincident(g87,g86)
    c: Coincident(g89,g88)
    c: Coincident(g90,g89)
    c: Coincident(g91,g90)
    c: Coincident(g93,g92)
    c: Coincident(g95,g94)
    c: Coincident(g97,g96)
    c: Coincident(g98,g97)
    c: Coincident(g99,g98)
    c: Coincident(g100,g99)
    c: Coincident(g104,g103)
    c: Coincident(g106,g105)
    c: Coincident(g107,g106)
    c: Coincident(g111,g110)
    c: Coincident(g113,g112)
    c: Coincident(g118,g117)
    c: Coincident(g122,g121)
    c: Coincident(g126,g125)
    c: Coincident(g130,g129)
    c: Coincident(g133,g132)
    c: Coincident(g134,g133)
    c: Coincident(g135,g134)
    c: Coincident(g139,g138)
    c: Coincident(g142,g141)
    c: Coincident(g156,g155)
    c: Coincident(g157,g156)
    c: Coincident(g159,g158)
    c: Coincident(g161,g160)
    c: Coincident(g164,g163)
    c: Coincident(g165,g164)
    c: Coincident(g168,g167)
    c: Coincident(g169,g168)
    c: Coincident(g171,g170)
    c: Coincident(g171,g0)
    c: Coincident(g172,g105)
    c: DistanceX(g165) = -12.4212
    c: DistanceY(g165) = -0.347049
    c: Coincident(g173,g0)
    c: Coincident(g173,g1)
    c: Coincident(g174,g1)
    c: Coincident(g177,g174)
    c: Coincident(g177,g175)
    c: Coincident(g178,g176)
    c: Coincident(g181,g2)
    c: Coincident(g182,g4)
    c: Coincident(g186,g185)
    c: Coincident(g186,g5)
    c: Coincident(g187,g16)
    c: Coincident(g187,g17)
    c: Coincident(g188,g21)
    c: Coincident(g188,g20)
    c: Coincident(g189,g28)
    c: Coincident(g189,g29)
    c: Coincident(g190,g29)
    c: Coincident(g190,g30)
    c: Coincident(g191,g42)
    c: Coincident(g191,g43)
    c: Coincident(g192,g63)
    c: Coincident(g192,g64)
    c: Coincident(g193,g66)
    c: Coincident(g193,g67)
    c: Coincident(g194,g92)
    c: Coincident(g194,g91)
    c: Coincident(g195,g119)
    c: Coincident(g195,g118)
    c: Coincident(g196,g120)
    c: Coincident(g197,g119)
    c: Coincident(g198,g129)
    c: Coincident(g198,g128)
    c: Coincident(g199,g131)
    c: Coincident(g200,g199)
    c: Coincident(g201,g130)
    c: Coincident(g201,g200)
    c: Coincident(g202,g132)
    c: Coincident(g202,g131)
    c: Coincident(g203,g172)
    c: Coincident(g203,g104)
    c: Coincident(g204,g103)
    c: Coincident(g204,g102)
FEATURE [PartDesign::Pad] Pad001
  Direction = (0,0,1)
  Length = 3
  Length2 = 10
  Profile = -> Sketch001
  ReferenceAxis = -> Sketch001 [N_Axis]
  Type = 0
FEATURE [PartDesign::Body] Body001  label="logo002"
  Group = -> [Sketch001,Pad001]
  Origin = -> Origin001
  Placement = pos=(39.35,-43,30) rot=(1,0,0;1.5708rad)
  Tip = -> Pad001
FEATURE [Part::MultiFuse] Fusion040  label="logo003"
  Placement = pos=(-69,-26,58) rot=(1,0,0;3.14159rad)
  Shapes = -> [Body001,Box068]
FEATURE [Part::Cut] Cut008  label="front002"
  Base = -> Cut003
  Tool = -> Fusion040
FEATURE [Part::Box] Box069  label="logoBase002"
  AttacherType = Attacher::AttachEngine3D
  Height = 30
  Length = 35
  Placement = pos=(21.5,-44,15.25) rot=(0,0,1;0rad)
  Width = 1.8
FEATURE [Sketcher::SketchObject] Sketch002
  FullyConstrained = false
  MapMode = 5
  Support = -> [XY_Plane002]
  sketch-geometry (205):
    g0: LineSegment StartX=-15.0667 StartY=-2.9879 StartZ=0 EndX=-14.4175 EndY=-3.20194 EndZ=0
    g1: LineSegment StartX=-14.1386 StartY=-3.3581 StartZ=0 EndX=-13.8673 EndY=-3.55064 EndZ=0
    g2: LineSegment StartX=-10.8098 StartY=-4.00788 StartZ=0 EndX=-10.5716 EndY=-4.29909 EndZ=0
    g3: LineSegment StartX=-10.5716 StartY=-4.29909 StartZ=0 EndX=-10.1338 EndY=-4.33136 EndZ=0
    g4: LineSegment StartX=-10.1338 StartY=-4.33136 StartZ=0 EndX=-9.89036 EndY=-4.3898 EndZ=0
    g5: LineSegment StartX=-9.51656 StartY=-5.73022 StartZ=0 EndX=-9.24931 EndY=-5.76229 EndZ=0
    g6: LineSegment StartX=-9.24931 StartY=-5.76229 StartZ=0 EndX=-8.92861 EndY=-5.90126 EndZ=0
    g7: LineSegment StartX=-8.92861 StartY=-5.90126 StartZ=0 EndX=-8.54378 EndY=-5.86384 EndZ=0
    g8: LineSegment StartX=-8.54378 StartY=-5.86384 StartZ=0 EndX=-7.71788 EndY=-5.75845 EndZ=0
    g9: LineSegment StartX=-7.71788 StartY=-5.75845 StartZ=0 EndX=-7.37291 EndY=-5.97257 EndZ=0
    g10: LineSegment StartX=-7.37291 StartY=-5.97257 StartZ=0 EndX=-6.72487 EndY=-5.72038 EndZ=0
    g11: LineSegment StartX=-6.72487 StartY=-5.72038 StartZ=0 EndX=-6.27066 EndY=-5.69481 EndZ=0
    g12: LineSegment StartX=-6.27066 StartY=-5.69481 StartZ=0 EndX=-6.06223 EndY=-5.80493 EndZ=0
    g13: LineSegment StartX=-6.06223 StartY=-5.80493 StartZ=0 EndX=-5.35089 EndY=-5.48914 EndZ=0
    g14: LineSegment StartX=-5.35089 StartY=-5.48914 StartZ=0 EndX=-5.02402 EndY=-5.48914 EndZ=0
    g15: LineSegment StartX=-5.02402 StartY=-5.48914 StartZ=0 EndX=-4.80126 EndY=-5.53132 EndZ=0
    g16: LineSegment StartX=-4.80126 StartY=-5.53132 StartZ=0 EndX=-4.19735 EndY=-5.16248 EndZ=0
    g17: LineSegment StartX=-3.75191 StartY=-4.97251 StartZ=0 EndX=-3.37714 EndY=-4.97251 EndZ=0
    g18: LineSegment StartX=-3.37714 StartY=-4.97251 StartZ=0 EndX=-2.81898 EndY=-4.45422 EndZ=0
    g19: LineSegment StartX=-2.81898 StartY=-4.45422 StartZ=0 EndX=-2.62761 EndY=-4.34259 EndZ=0
    g20: LineSegment StartX=-2.62761 StartY=-4.34259 StartZ=0 EndX=-2.15112 EndY=-4.35765 EndZ=0
    g21: LineSegment StartX=-2.38042 StartY=-4.51801 StartZ=0 EndX=-3.18577 EndY=-5.42702 EndZ=0
    g22: LineSegment StartX=-3.18577 StartY=-5.42702 StartZ=0 EndX=-3.61318 EndY=-6.05824 EndZ=0
    g23: LineSegment StartX=-3.61318 StartY=-6.05824 StartZ=0 EndX=-3.7111 EndY=-6.64579 EndZ=0
    g24: LineSegment StartX=-3.7111 StartY=-6.64579 StartZ=0 EndX=-3.83514 EndY=-7.15501 EndZ=0
    g25: LineSegment StartX=-3.83514 StartY=-7.15501 StartZ=0 EndX=-3.75878 EndY=-7.50876 EndZ=0
    g26: LineSegment StartX=-3.75878 StartY=-7.50876 StartZ=0 EndX=-3.70596 EndY=-7.68135 EndZ=0
    g27: LineSegment StartX=-3.70596 StartY=-7.68135 StartZ=0 EndX=-3.53967 EndY=-7.85202 EndZ=0
    g28: LineSegment StartX=-3.53967 StartY=-7.85202 StartZ=0 EndX=-3.4685 EndY=-8.65617 EndZ=0
    g29: LineSegment StartX=-3.27268 StartY=-8.56671 StartZ=0 EndX=-3.16823 EndY=-8.76909 EndZ=0
    g30: LineSegment StartX=-3.07088 StartY=-9.32083 StartZ=0 EndX=-2.84207 EndY=-9.3355 EndZ=0
    g31: LineSegment StartX=-2.84207 StartY=-9.3355 StartZ=0 EndX=-2.45193 EndY=-10.0982 EndZ=0
    g32: LineSegment StartX=-2.45193 StartY=-10.0982 StartZ=0 EndX=-2.24953 EndY=-10.1304 EndZ=0
    g33: LineSegment StartX=-2.24953 StartY=-10.1304 StartZ=0 EndX=-0.96042 EndY=-11.8753 EndZ=0
    g34: LineSegment StartX=-0.96042 StartY=-11.8753 StartZ=0 EndX=-0.153326 EndY=-11.3889 EndZ=0
    g35: LineSegment StartX=-0.153326 StartY=-11.3889 StartZ=0 EndX=0.461347 EndY=-10.7689 EndZ=0
    g36: LineSegment StartX=0.461347 StartY=-10.7689 StartZ=0 EndX=0.669802 EndY=-10.7261 EndZ=0
    g37: LineSegment StartX=0.669802 StartY=-10.7261 StartZ=0 EndX=1.31724 EndY=-9.70998 EndZ=0
    g38: LineSegment StartX=1.31724 StartY=-9.70998 StartZ=0 EndX=1.51826 EndY=-9.65081 EndZ=0
    g39: LineSegment StartX=1.51826 StartY=-9.65081 StartZ=0 EndX=1.74022 EndY=-9.08937 EndZ=0
    g40: LineSegment StartX=1.74022 StartY=-9.08937 StartZ=0 EndX=2.02094 EndY=-9.04367 EndZ=0
    g41: LineSegment StartX=2.02094 StartY=-9.04367 StartZ=0 EndX=2.39306 EndY=-7.80327 EndZ=0
    g42: LineSegment StartX=2.39306 StartY=-7.80327 StartZ=0 EndX=2.58839 EndY=-7.69871 EndZ=0
    g43: LineSegment StartX=2.6542 StartY=-7.03945 StartZ=0 EndX=2.86963 EndY=-6.81749 EndZ=0
    g44: LineSegment StartX=2.86963 StartY=-6.81749 StartZ=0 EndX=3.0916 EndY=-6.92847 EndZ=0
    g45: LineSegment StartX=3.0916 StartY=-6.92847 StartZ=0 EndX=3.79666 EndY=-7.57478 EndZ=0
    g46: LineSegment StartX=3.79666 StartY=-7.57478 StartZ=0 EndX=3.93376 EndY=-7.50297 EndZ=0
    g47: LineSegment StartX=3.93376 StartY=-7.50297 StartZ=0 EndX=4.46256 EndY=-7.97301 EndZ=0
    g48: LineSegment StartX=4.46256 StartY=-7.97301 StartZ=0 EndX=4.68452 EndY=-7.92079 EndZ=0
    g49: LineSegment StartX=4.68452 StartY=-7.92079 StartZ=0 EndX=5.1154 EndY=-8.34513 EndZ=0
    g50: LineSegment StartX=5.1154 StartY=-8.34513 StartZ=0 EndX=5.32431 EndY=-8.28637 EndZ=0
    g51: LineSegment StartX=5.32431 StartY=-8.28637 StartZ=0 EndX=6.23668 EndY=-8.79564 EndZ=0
    g52: LineSegment StartX=6.23668 StartY=-8.79564 StartZ=0 EndX=6.50362 EndY=-8.76631 EndZ=0
    g53: LineSegment StartX=6.50362 StartY=-8.76631 StartZ=0 EndX=7.14802 EndY=-9.05537 EndZ=0
    g54: LineSegment StartX=7.14802 StartY=-9.05537 StartZ=0 EndX=8.04883 EndY=-9.18613 EndZ=0
    g55: LineSegment StartX=8.04883 StartY=-9.18613 StartZ=0 EndX=8.36847 EndY=-7.93662 EndZ=0
    g56: LineSegment StartX=8.36847 StartY=-7.93662 StartZ=0 EndX=8.49923 EndY=-7.79133 EndZ=0
    g57: LineSegment StartX=8.49923 StartY=-7.79133 StartZ=0 EndX=8.43477 EndY=-6.72206 EndZ=0
    g58: LineSegment StartX=8.43477 StartY=-6.72206 StartZ=0 EndX=8.58621 EndY=-6.47988 EndZ=0
    g59: LineSegment StartX=8.58621 StartY=-6.47988 StartZ=0 EndX=8.32296 EndY=-5.53178 EndZ=0
    g60: LineSegment StartX=8.32296 StartY=-5.53178 StartZ=0 EndX=8.43984 EndY=-5.19091 EndZ=0
    g61: LineSegment StartX=8.43984 StartY=-5.19091 StartZ=0 EndX=8.07426 EndY=-4.39307 EndZ=0
    g62: LineSegment StartX=8.07426 StartY=-4.39307 StartZ=0 EndX=8.04236 EndY=-4.17777 EndZ=0
    g63: LineSegment StartX=8.04236 StartY=-4.17777 StartZ=0 EndX=8.0902 EndY=-3.99438 EndZ=0
    g64: LineSegment StartX=8.4103 StartY=-4.11103 StartZ=0 EndX=8.72013 EndY=-4.0502 EndZ=0
    g65: LineSegment StartX=8.72013 StartY=-4.0502 StartZ=0 EndX=9.31817 EndY=-4.0502 EndZ=0
    g66: LineSegment StartX=9.31817 StartY=-4.0502 StartZ=0 EndX=9.82964 EndY=-4.15887 EndZ=0
    g67: LineSegment StartX=10.1326 StartY=-3.9675 StartZ=0 EndX=10.5175 EndY=-3.9623 EndZ=0
    g68: LineSegment StartX=10.5175 StartY=-3.9623 StartZ=0 EndX=10.8831 EndY=-3.97536 EndZ=0
    g69: LineSegment StartX=10.8831 StartY=-3.97536 StartZ=0 EndX=11.2245 EndY=-4.09431 EndZ=0
    g70: LineSegment StartX=11.2245 StartY=-4.09431 StartZ=0 EndX=11.6861 EndY=-3.91007 EndZ=0
    g71: LineSegment StartX=11.6861 StartY=-3.91007 StartZ=0 EndX=12.1039 EndY=-3.88396 EndZ=0
    g72: LineSegment StartX=12.1039 StartY=-3.88396 StartZ=0 EndX=12.6 EndY=-3.9623 EndZ=0
    g73: LineSegment StartX=12.6 StartY=-3.9623 StartZ=0 EndX=13.5793 EndY=-3.87743 EndZ=0
    g74: LineSegment StartX=13.5793 StartY=-3.87743 StartZ=0 EndX=14.3888 EndY=-3.74687 EndZ=0
    g75: LineSegment StartX=14.3888 StartY=-3.74687 StartZ=0 EndX=14.7544 EndY=-3.68158 EndZ=0
    g76: LineSegment StartX=14.7544 StartY=-3.68158 StartZ=0 EndX=15.2767 EndY=-3.75339 EndZ=0
    g77: LineSegment StartX=15.2767 StartY=-3.75339 StartZ=0 EndX=15.0432 EndY=-3.24137 EndZ=0
    g78: LineSegment StartX=15.0432 StartY=-3.24137 StartZ=0 EndX=14.5209 EndY=-2.51672 EndZ=0
    g79: LineSegment StartX=14.5209 StartY=-2.51672 StartZ=0 EndX=14.0378 EndY=-1.99445 EndZ=0
    g80: LineSegment StartX=14.0378 StartY=-1.99445 StartZ=0 EndX=13.2802 EndY=-1.54625 EndZ=0
    g81: LineSegment StartX=13.2802 StartY=-1.54625 StartZ=0 EndX=13.0438 EndY=-1.23117 EndZ=0
    g82: LineSegment StartX=13.0438 StartY=-1.23117 StartZ=0 EndX=12.1074 EndY=-0.797939 EndZ=0
    g83: LineSegment StartX=12.1074 StartY=-0.797939 StartZ=0 EndX=11.3804 EndY=-0.250878 EndZ=0
    g84: LineSegment StartX=11.3804 StartY=-0.250878 StartZ=0 EndX=10.4396 EndY=0.304889 EndZ=0
    g85: LineSegment StartX=10.4396 StartY=0.304889 StartZ=0 EndX=9.59526 EndY=0.727998 EndZ=0
    g86: LineSegment StartX=9.59526 StartY=0.727998 StartZ=0 EndX=8.53624 EndY=0.97306 EndZ=0
    g87: LineSegment StartX=8.53624 StartY=0.97306 StartZ=0 EndX=7.199 EndY=0.97306 EndZ=0
    g88: LineSegment StartX=7.199 StartY=0.97306 StartZ=0 EndX=5.77932 EndY=0.795578 EndZ=0
    g89: LineSegment StartX=5.77932 StartY=0.795578 StartZ=0 EndX=5.60186 EndY=0.795578 EndZ=0
    g90: LineSegment StartX=5.60186 StartY=0.795578 StartZ=0 EndX=5.83178 EndY=0.981815 EndZ=0
    g91: LineSegment StartX=5.83178 StartY=0.981815 StartZ=0 EndX=6.25403 EndY=1.1582 EndZ=0
    g92: LineSegment StartX=6.30214 StartY=1.38269 StartZ=0 EndX=7.17987 EndY=1.70686 EndZ=0
    g93: LineSegment StartX=7.17987 StartY=1.70686 StartZ=0 EndX=7.44682 EndY=1.79438 EndZ=0
    g94: LineSegment StartX=7.44682 StartY=1.79438 StartZ=0 EndX=7.49058 EndY=2.12696 EndZ=0
    g95: LineSegment StartX=7.49058 StartY=2.12696 StartZ=0 EndX=8.30058 EndY=2.66839 EndZ=0
    g96: LineSegment StartX=8.30058 StartY=2.66839 StartZ=0 EndX=8.68575 EndY=2.81854 EndZ=0
    g97: LineSegment StartX=8.68575 StartY=2.81854 StartZ=0 EndX=8.68575 EndY=3.12537 EndZ=0
    g98: LineSegment StartX=8.68575 StartY=3.12537 StartZ=0 EndX=8.89508 EndY=3.18684 EndZ=0
    g99: LineSegment StartX=8.89508 StartY=3.18684 StartZ=0 EndX=9.63492 EndY=4.06602 EndZ=0
    g100: LineSegment StartX=9.63492 StartY=4.06602 StartZ=0 EndX=9.62638 EndY=4.32743 EndZ=0
    g101: LineSegment StartX=9.62638 StartY=4.32743 StartZ=0 EndX=10.2068 EndY=5.18314 EndZ=0
    g102: LineSegment StartX=10.2068 StartY=5.18314 StartZ=0 EndX=9.25518 EndY=5.64445 EndZ=0
    g103: LineSegment StartX=9.1102 StartY=5.87597 StartZ=0 EndX=8.32132 EndY=5.97336 EndZ=0
    g104: LineSegment StartX=8.32132 StartY=5.97336 StartZ=0 EndX=8.15466 EndY=6.06625 EndZ=0
    g105: LineSegment StartX=7.63471 StartY=6.13088 StartZ=0 EndX=7.56391 EndY=6.33267 EndZ=0
    g106: LineSegment StartX=7.56391 StartY=6.33267 StartZ=0 EndX=6.74832 EndY=6.35496 EndZ=0
    g107: LineSegment StartX=6.74832 StartY=6.35496 StartZ=0 EndX=6.46819 EndY=6.29526 EndZ=0
    g108: LineSegment StartX=6.46819 StartY=6.29526 StartZ=0 EndX=6.27042 EndY=6.61061 EndZ=0
    g109: LineSegment StartX=6.27042 StartY=6.61061 StartZ=0 EndX=5.40453 EndY=6.33267 EndZ=0
    g110: LineSegment StartX=5.40453 StartY=6.33267 StartZ=0 EndX=5.27091 EndY=6.47164 EndZ=0
    g111: LineSegment StartX=5.27091 StartY=6.47164 StartZ=0 EndX=4.56942 EndY=6.24725 EndZ=0
    g112: LineSegment StartX=4.56942 StartY=6.24725 StartZ=0 EndX=4.44161 EndY=6.40652 EndZ=0
    g113: LineSegment StartX=4.44161 StartY=6.40652 StartZ=0 EndX=3.4195 EndY=5.94588 EndZ=0
    g114: LineSegment StartX=3.4195 StartY=5.94588 StartZ=0 EndX=3.29192 EndY=6.1532 EndZ=0
    g115: LineSegment StartX=3.29192 StartY=6.1532 StartZ=0 EndX=2.15964 EndY=5.49137 EndZ=0
    g116: LineSegment StartX=2.15964 StartY=5.49137 StartZ=0 EndX=2.00016 EndY=5.69869 EndZ=0
    g117: LineSegment StartX=2.00016 StartY=5.69869 StartZ=0 EndX=1.6185 EndY=5.34828 EndZ=0
    g118: LineSegment StartX=1.6185 StartY=5.34828 StartZ=0 EndX=1.45984 EndY=5.94974 EndZ=0
    g119: LineSegment StartX=1.38165 StartY=6.28651 StartZ=0 EndX=1.14534 EndY=6.29963 EndZ=0
    g120: LineSegment StartX=0.348522 StartY=7.29544 StartZ=0 EndX=0.126706 EndY=7.68126 EndZ=0
    g121: LineSegment StartX=0.126706 StartY=7.68126 StartZ=0 EndX=-0.415308 EndY=8.18163 EndZ=0
    g122: LineSegment StartX=-0.415308 StartY=8.18163 StartZ=0 EndX=-0.872658 EndY=8.6237 EndZ=0
    g123: LineSegment StartX=-0.872658 StartY=8.6237 StartZ=0 EndX=-1.12074 EndY=8.64329 EndZ=0
    g124: LineSegment StartX=-1.12074 StartY=8.64329 StartZ=0 EndX=-1.79316 EndY=9.11986 EndZ=0
    g125: LineSegment StartX=-1.79316 StartY=9.11986 StartZ=0 EndX=-2.31488 EndY=9.12122 EndZ=0
    g126: LineSegment StartX=-2.31488 StartY=9.12122 StartZ=0 EndX=-2.71321 EndY=9.13846 EndZ=0
    g127: LineSegment StartX=-2.71321 StartY=9.13846 StartZ=0 EndX=-2.88425 EndY=9.34157 EndZ=0
    g128: LineSegment StartX=-2.88425 StartY=9.34157 StartZ=0 EndX=-3.16779 EndY=9.26454 EndZ=0
    g129: LineSegment StartX=-3.70739 StartY=9.82796 StartZ=0 EndX=-4.04915 EndY=9.7003 EndZ=0
    g130: LineSegment StartX=-4.04915 StartY=9.7003 StartZ=0 EndX=-4.42988 EndY=10.011 EndZ=0
    g131: LineSegment StartX=-5.98947 StartY=10.3656 StartZ=0 EndX=-7.32605 EndY=10.4108 EndZ=0
    g132: LineSegment StartX=-7.25254 StartY=9.13254 StartZ=0 EndX=-7.36878 EndY=8.7693 EndZ=0
    g133: LineSegment StartX=-7.36878 StartY=8.7693 StartZ=0 EndX=-7.2614 EndY=7.83762 EndZ=0
    g134: LineSegment StartX=-7.2614 StartY=7.83762 StartZ=0 EndX=-7.41112 EndY=7.6042 EndZ=0
    g135: LineSegment StartX=-7.41112 StartY=7.6042 StartZ=0 EndX=-7.09216 EndY=6.74302 EndZ=0
    g136: LineSegment StartX=-7.09216 StartY=6.74302 StartZ=0 EndX=-7.10014 EndY=6.55962 EndZ=0
    g137: LineSegment StartX=-7.10014 StartY=6.55962 StartZ=0 EndX=-7.29151 EndY=6.3842 EndZ=0
    g138: LineSegment StartX=-7.29151 StartY=6.3842 StartZ=0 EndX=-6.74132 EndY=5.29976 EndZ=0
    g139: LineSegment StartX=-6.74132 StartY=5.29976 StartZ=0 EndX=-6.87495 EndY=5.02732 EndZ=0
    g140: LineSegment StartX=-6.87495 StartY=5.02732 StartZ=0 EndX=-6.31586 EndY=4.42065 EndZ=0
    g141: LineSegment StartX=-6.31586 StartY=4.42065 StartZ=0 EndX=-6.30396 EndY=4.19463 EndZ=0
    g142: LineSegment StartX=-6.30396 StartY=4.19463 StartZ=0 EndX=-6.05415 EndY=4.0043 EndZ=0
    g143: LineSegment StartX=-6.05415 StartY=4.0043 StartZ=0 EndX=-6.18501 EndY=3.95672 EndZ=0
    g144: LineSegment StartX=-6.18501 StartY=3.95672 StartZ=0 EndX=-5.54265 EndY=3.07645 EndZ=0
    g145: LineSegment StartX=-5.54265 StartY=3.07645 StartZ=0 EndX=-5.57833 EndY=2.90991 EndZ=0
    g146: LineSegment StartX=-5.57833 StartY=2.90991 StartZ=0 EndX=-5.1263 EndY=2.41029 EndZ=0
    g147: LineSegment StartX=-5.1263 StartY=2.41029 StartZ=0 EndX=-5.18578 EndY=2.26755 EndZ=0
    g148: LineSegment StartX=-5.18578 StartY=2.26755 StartZ=0 EndX=-4.73375 EndY=1.89878 EndZ=0
    g149: LineSegment StartX=-4.73375 StartY=1.89878 StartZ=0 EndX=-4.42446 EndY=1.5895 EndZ=0
    g150: LineSegment StartX=-4.42446 StartY=1.5895 StartZ=0 EndX=-5.31663 EndY=1.29211 EndZ=0
    g151: LineSegment StartX=-5.31663 StartY=1.29211 StartZ=0 EndX=-5.84004 EndY=1.08988 EndZ=0
    g152: LineSegment StartX=-5.84004 StartY=1.08988 StartZ=0 EndX=-6.04226 EndY=0.792495 EndZ=0
    g153: LineSegment StartX=-6.04226 StartY=0.792495 StartZ=0 EndX=-6.94632 EndY=0.994719 EndZ=0
    g154: LineSegment StartX=-6.94632 StartY=0.994719 StartZ=0 EndX=-7.19613 EndY=0.887659 EndZ=0
    g155: LineSegment StartX=-7.19613 StartY=0.887659 StartZ=0 EndX=-7.8147 EndY=1.0423 EndZ=0
    g156: LineSegment StartX=-7.8147 StartY=1.0423 StartZ=0 EndX=-8.02502 EndY=0.969153 EndZ=0
    g157: LineSegment StartX=-8.02502 StartY=0.969153 StartZ=0 EndX=-8.60267 EndY=1.03042 EndZ=0
    g158: LineSegment StartX=-8.60267 StartY=1.03042 StartZ=0 EndX=-8.8346 EndY=0.872878 EndZ=0
    g159: LineSegment StartX=-8.8346 StartY=0.872878 StartZ=0 EndX=-9.33349 EndY=0.929767 EndZ=0
    g160: LineSegment StartX=-9.33349 StartY=0.929767 StartZ=0 EndX=-9.66169 EndY=0.649695 EndZ=0
    g161: LineSegment StartX=-9.66169 StartY=0.649695 StartZ=0 EndX=-10.3249 EndY=0.649695 EndZ=0
    g162: LineSegment StartX=-10.3249 StartY=0.649695 StartZ=0 EndX=-11.0107 EndY=0.32425 EndZ=0
    g163: LineSegment StartX=-11.0107 StartY=0.32425 StartZ=0 EndX=-11.7283 EndY=0.053139 EndZ=0
    g164: LineSegment StartX=-11.7283 StartY=0.053139 StartZ=0 EndX=-12.2971 EndY=-0.13161 EndZ=0
    g165: LineSegment StartX=-12.2971 StartY=-0.13161 StartZ=0 EndX=-12.4212 EndY=-0.347049 EndZ=0
    g166: LineSegment StartX=-12.4212 StartY=-0.347049 StartZ=0 EndX=-13.296 EndY=-0.817096 EndZ=0
    g167: LineSegment StartX=-13.296 StartY=-0.817096 StartZ=0 EndX=-13.9227 EndY=-1.24144 EndZ=0
    g168: LineSegment StartX=-13.9227 StartY=-1.24144 StartZ=0 EndX=-14.1708 EndY=-1.59398 EndZ=0
    g169: LineSegment StartX=-14.1708 StartY=-1.59398 StartZ=0 EndX=-14.5386 EndY=-2.09216 EndZ=0
    g170: LineSegment StartX=-14.5386 StartY=-2.09216 StartZ=0 EndX=-14.7831 EndY=-2.4577 EndZ=0
    g171: LineSegment StartX=-14.7831 StartY=-2.4577 StartZ=0 EndX=-15.0667 EndY=-2.9879 EndZ=0
    g172: LineSegment StartX=7.82861 StartY=6.04487 StartZ=0 EndX=7.63471 EndY=6.13088 EndZ=0
    g173: LineSegment StartX=-14.4175 StartY=-3.20194 StartZ=0 EndX=-14.1386 EndY=-3.3581 EndZ=0
    g174: LineSegment StartX=-13.8673 StartY=-3.55064 StartZ=0 EndX=-13.4107 EndY=-3.57136 EndZ=0
    g175: LineSegment StartX=-13.1321 StartY=-3.61699 StartZ=0 EndX=-12.817 EndY=-3.62343 EndZ=0
    g176: LineSegment StartX=-12.817 StartY=-3.62343 StartZ=0 EndX=-12.4662 EndY=-3.85302 EndZ=0
    g177: LineSegment StartX=-13.4107 StartY=-3.57136 StartZ=0 EndX=-13.1321 EndY=-3.61699 EndZ=0
    g178: LineSegment StartX=-12.4662 StartY=-3.85302 StartZ=0 EndX=-11.8704 EndY=-3.85302 EndZ=0
    g179: LineSegment StartX=-11.8704 StartY=-3.85302 StartZ=0 EndX=-11.5204 EndY=-4.00836 EndZ=0
    g180: LineSegment StartX=-11.5204 StartY=-4.00836 StartZ=0 EndX=-11.1389 EndY=-4.05555 EndZ=0
    g181: LineSegment StartX=-11.1389 StartY=-4.05555 StartZ=0 EndX=-10.8098 EndY=-4.00788 EndZ=0
    g182: LineSegment StartX=-9.89036 StartY=-4.3898 StartZ=0 EndX=-9.99555 EndY=-4.87697 EndZ=0
    g183: LineSegment StartX=-9.99555 StartY=-4.87697 StartZ=0 EndX=-10.0894 EndY=-5.36391 EndZ=0
    g184: LineSegment StartX=-10.0894 StartY=-5.36391 StartZ=0 EndX=-10.107 EndY=-5.50471 EndZ=0
    g185: LineSegment StartX=-10.107 StartY=-5.50471 StartZ=0 EndX=-9.77848 EndY=-5.63965 EndZ=0
    g186: LineSegment StartX=-9.77848 StartY=-5.63965 StartZ=0 EndX=-9.51656 EndY=-5.73022 EndZ=0
    g187: LineSegment StartX=-4.19735 StartY=-5.16248 StartZ=0 EndX=-3.75191 EndY=-4.97251 EndZ=0
    g188: LineSegment StartX=-2.38042 StartY=-4.51801 StartZ=0 EndX=-2.15112 EndY=-4.35765 EndZ=0
    g189: LineSegment StartX=-3.4685 StartY=-8.65617 StartZ=0 EndX=-3.27268 EndY=-8.56671 EndZ=0
    g190: LineSegment StartX=-3.16823 StartY=-8.76909 StartZ=0 EndX=-3.07088 EndY=-9.32083 EndZ=0
    g191: LineSegment StartX=2.58839 StartY=-7.69871 StartZ=0 EndX=2.6542 EndY=-7.03945 EndZ=0
    g192: LineSegment StartX=8.0902 StartY=-3.99438 StartZ=0 EndX=8.4103 EndY=-4.11103 EndZ=0
    g193: LineSegment StartX=9.82964 StartY=-4.15887 StartZ=0 EndX=10.1326 EndY=-3.9675 EndZ=0
    g194: LineSegment StartX=6.30214 StartY=1.38269 StartZ=0 EndX=6.25403 EndY=1.1582 EndZ=0
    g195: LineSegment StartX=1.38165 StartY=6.28651 StartZ=0 EndX=1.45984 EndY=5.94974 EndZ=0
    g196: LineSegment StartX=0.348522 StartY=7.29544 StartZ=0 EndX=0.824344 EndY=6.91479 EndZ=0
    g197: LineSegment StartX=0.824344 StartY=6.91479 StartZ=0 EndX=1.14534 EndY=6.29963 EndZ=0
    g198: LineSegment StartX=-3.70739 StartY=9.82796 StartZ=0 EndX=-3.16779 EndY=9.26454 EndZ=0
    g199: LineSegment StartX=-5.98947 StartY=10.3656 StartZ=0 EndX=-5.43038 EndY=10.4489 EndZ=0
    g200: LineSegment StartX=-5.43038 StartY=10.4489 StartZ=0 EndX=-4.9791 EndY=10.1425 EndZ=0
    g201: LineSegment StartX=-4.42988 StartY=10.011 StartZ=0 EndX=-4.9791 EndY=10.1425 EndZ=0
    g202: LineSegment StartX=-7.25254 StartY=9.13254 StartZ=0 EndX=-7.32605 EndY=10.4108 EndZ=0
    g203: LineSegment StartX=7.82861 StartY=6.04487 StartZ=0 EndX=8.15466 EndY=6.06625 EndZ=0
    g204: LineSegment StartX=9.1102 StartY=5.87597 StartZ=0 EndX=9.25518 EndY=5.64445 EndZ=0
  constraints (114):
    c: Coincident(g4,g3)
    c: Coincident(g6,g5)
    c: Coincident(g8,g7)
    c: Coincident(g9,g8)
    c: Coincident(g10,g9)
    c: Coincident(g11,g10)
    c: Coincident(g13,g12)
    c: Coincident(g16,g15)
    c: Coincident(g22,g21)
    c: Coincident(g25,g24)
    c: Coincident(g26,g25)
    c: Coincident(g28,g27)
    c: Coincident(g33,g32)
    c: Coincident(g37,g36)
    c: Coincident(g38,g37)
    c: Coincident(g40,g39)
    c: Coincident(g44,g43)
    c: Coincident(g51,g50)
    c: Coincident(g52,g51)
    c: Coincident(g57,g56)
    c: Coincident(g58,g57)
    c: Coincident(g59,g58)
    c: Coincident(g61,g60)
    c: Coincident(g63,g62)
    c: Coincident(g66,g65)
    c: Coincident(g70,g69)
    c: Coincident(g72,g71)
    c: Coincident(g73,g72)
    c: Coincident(g74,g73)
    c: Coincident(g77,g76)
    c: Coincident(g80,g79)
    c: Coincident(g81,g80)
    c: Coincident(g83,g82)
    c: Coincident(g85,g84)
    c: Coincident(g86,g85)
    c: Coincident(g87,g86)
    c: Coincident(g89,g88)
    c: Coincident(g90,g89)
    c: Coincident(g91,g90)
    c: Coincident(g93,g92)
    c: Coincident(g95,g94)
    c: Coincident(g97,g96)
    c: Coincident(g98,g97)
    c: Coincident(g99,g98)
    c: Coincident(g100,g99)
    c: Coincident(g104,g103)
    c: Coincident(g106,g105)
    c: Coincident(g107,g106)
    c: Coincident(g111,g110)
    c: Coincident(g113,g112)
    c: Coincident(g118,g117)
    c: Coincident(g122,g121)
    c: Coincident(g126,g125)
    c: Coincident(g130,g129)
    c: Coincident(g133,g132)
    c: Coincident(g134,g133)
    c: Coincident(g135,g134)
    c: Coincident(g139,g138)
    c: Coincident(g142,g141)
    c: Coincident(g156,g155)
    c: Coincident(g157,g156)
    c: Coincident(g159,g158)
    c: Coincident(g161,g160)
    c: Coincident(g164,g163)
    c: Coincident(g165,g164)
    c: Coincident(g168,g167)
    c: Coincident(g169,g168)
    c: Coincident(g171,g170)
    c: Coincident(g171,g0)
    c: Coincident(g172,g105)
    c: DistanceX(g165) = -12.4212
    c: DistanceY(g165) = -0.347049
    c: Coincident(g173,g0)
    c: Coincident(g173,g1)
    c: Coincident(g174,g1)
    c: Coincident(g177,g174)
    c: Coincident(g177,g175)
    c: Coincident(g178,g176)
    c: Coincident(g181,g2)
    c: Coincident(g182,g4)
    c: Coincident(g186,g185)
    c: Coincident(g186,g5)
    c: Coincident(g187,g16)
    c: Coincident(g187,g17)
    c: Coincident(g188,g21)
    c: Coincident(g188,g20)
    c: Coincident(g189,g28)
    c: Coincident(g189,g29)
    c: Coincident(g190,g29)
    c: Coincident(g190,g30)
    c: Coincident(g191,g42)
    c: Coincident(g191,g43)
    c: Coincident(g192,g63)
    c: Coincident(g192,g64)
    c: Coincident(g193,g66)
    c: Coincident(g193,g67)
    c: Coincident(g194,g92)
    c: Coincident(g194,g91)
    c: Coincident(g195,g119)
    c: Coincident(g195,g118)
    c: Coincident(g196,g120)
    c: Coincident(g197,g119)
    c: Coincident(g198,g129)
    c: Coincident(g198,g128)
    c: Coincident(g199,g131)
    c: Coincident(g200,g199)
    c: Coincident(g201,g130)
    c: Coincident(g201,g200)
    c: Coincident(g202,g132)
    c: Coincident(g202,g131)
    c: Coincident(g203,g172)
    c: Coincident(g203,g104)
    c: Coincident(g204,g103)
    c: Coincident(g204,g102)
FEATURE [PartDesign::Pad] Pad002
  Direction = (0,0,1)
  Length = 3
  Length2 = 10
  Profile = -> Sketch002
  ReferenceAxis = -> Sketch002 [N_Axis]
  Type = 0
FEATURE [PartDesign::Body] Body002  label="logo004"
  Group = -> [Sketch002,Pad002]
  Origin = -> Origin002
  Placement = pos=(39.35,-43,30) rot=(1,0,0;1.5708rad)
  Tip = -> Pad002
FEATURE [Part::MultiFuse] Fusion041  label="logo"
  Placement = pos=(-69,-26,58) rot=(1,0,0;3.14159rad)
  Shapes = -> [Body002,Box069]
FEATURE [Part::MultiFuse] Fusion006  label="back001"
  Shapes = -> [Cut007,Box021]
FEATURE [Part::MultiFuse] Fusion042
  Shapes = -> [Fusion006,Cut008]
FEATURE [Part::Cylinder] Cylinder011
  Angle = 90
  AttacherType = Attacher::AttachEngine3D
  FirstAngle = 0
  Height = 65.2
  Placement = pos=(-50,18,-45.4) rot=(0,0,1;1.5708rad)
  Radius = 2
  SecondAngle = 0
FEATURE [Part::Box] Box070  label="Cube010"
  AttacherType = Attacher::AttachEngine3D
  Height = 20
  Length = 1.7
  Placement = pos=(-50.3,0.2,-10) rot=(0,1,0;3.14159rad)
  Width = 17.8
